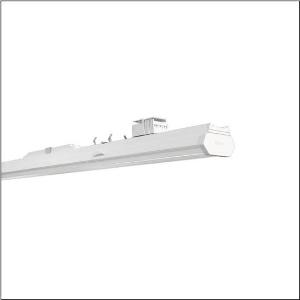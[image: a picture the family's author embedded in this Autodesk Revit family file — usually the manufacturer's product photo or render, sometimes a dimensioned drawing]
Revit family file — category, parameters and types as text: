
# Revit family: licross_r__21_protected_mo_52td1bvn465g_e1b8
name_source: partatom
category: Lighting Fixtures
units: mm (PartAtom-declared; Revit-internal decimal feet)

## family parameters
Cut with Voids When Loaded = No
Host = Face
Light Source = No
Part Type = Normal
Room Calculation Point = No
Round Connector Dimension = Use Diameter
Shared = No

## types (1)
- --- (1 x LED, 6500 lm, 39 W, 4000K)
    Apparent Load = 39 VA
    CIE Flux Codes = 54 82 95 97 100
    Color Rendering = 80
    Color Temperature = 4000K
    Default Elevation = 1800 mm
    Description = Licross® 21 Protected MO, luminaire insert, of sheet steel, galvanised, coil coated, white, length: 1.500mm, width: 90mm, height: 101mm, LED rated luminous flux: 6.500lm, light colour: 840, control gear: DALI 2, CLO, with plug, 5-pole, with phase selection, mains connection: 220..240V, AC, 50/60Hz, start of lifetime: 39W, end of service life: 46W, halogen-free wiring, primary optical cover: cover, of PMMA, light emission: direct distribution, primary light characteristic: symmetric, protection rating (complete): IP54, insulation class (complete): insulation class I (protective earthing), certification: CE, ENEC, VDE, UKCA, protection symbol: D if used in an environment with non-conductive dust loads with corresponding accessories, impact resistance: IK06, permissible ambient temperature for indoor applications: -25..+45°C, corresponds to IFS (International Featured Standards) requirements for safety and quality in the food industry, reducing of maximum allowable ambient temperature of 5°C with ceiling mounting, LABS conformity tested according to VDMA 24364:2018-05, packaging unit: 1 piece
    Height = 92 mm
    Lamp = 1 x LED
    Lamp Light Flux = 6500 lm
    Lamp Power = 39 W
    Lamp count = 1
    Length = 1500 mm
    Luminous efficacy = 167 lm/W
    Manufacturer = Siteco
    ModVariant = No
    Model = 52TD1BVN465G
    Mounting Place = Ceiling
    Mounting Type = Pendant
    Number of Poles = 1
    OnlyDefault = Yes
    Power Factor = 1
    Product Name = Licross® 21 Protected MO
    Product group = luminaire insert
    ProductGroupID = 901
    Protection Class = Protection class I
    Protection Degree = IP 54
    RLX_Detail_Level = 1
    RLX_Emergency_Light_Flux = 0 lm
    RLX_Emergency_Type = 0
    RLX_Emergency_Type_DB = No
    RlxData = <blob elided: 24361 chars, md5=277e41af>
    Socket = socket
    Standby Power = 0 W
    System Light Flux = 6500 lm
    System Power = 39 W
    Type Comments = factory setting: luminous flux: 100 % | dim-lin: 254 | 262 mA
    Type Image = l_1256148.jpg
    URL = http://relux.com
    VarID = @adj_052143
    Voltage = 0 V
    Weight = 0.00 kg
    Width = 88 mm

## geometry (parser evidence)
native form markers: Blend x4, Sweep x10
no freeform markers — native parametric forms only
